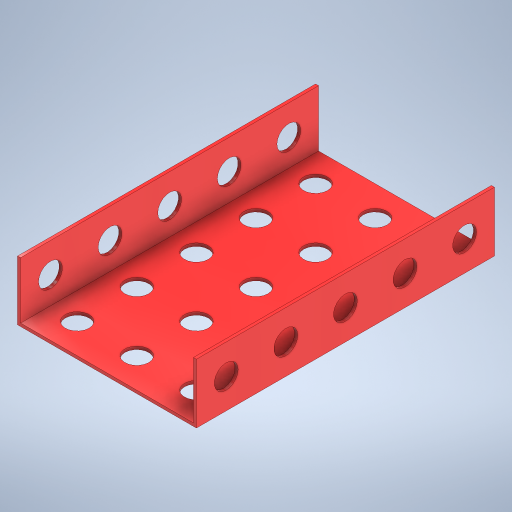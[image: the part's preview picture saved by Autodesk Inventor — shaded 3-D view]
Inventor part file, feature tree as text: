
AUTODESK INVENTOR PART (.ipt)
format: ipt  version: 2024 (Build 280153000, 153)  size: 333,312 bytes
history: native  units: mm
features: extrude x3, sketch x3, pattern_linear x2, other x1
ambient origin geometry x8: Origin, YZ Plane, XZ Plane, XY Plane, X Axis, Y Axis, Z Axis, Center Point
bodies: Body1 (feature_tree)
feature tree (9):
  other  "Těleso1"
  extrude  "Vysunutí1"  Depth=15.0mm
  extrude  "Vysunutí2"  Depth=15.0mm
  pattern_linear  "Obdélníkové pole1"  Spacing1=0.5mm  [1 undecoded]
  extrude  "Vysunutí3"  Depth=0.5mm
  pattern_linear  "Obdélníkové pole2"  Spacing1=0.5mm  [1 undecoded]
  sketch  "Náčrt1"
  sketch  "Náčrt2"
  sketch  "Náčrt3"
note: 2 required parameter values undecoded (feature->parameter linkage not recoverable at this tier; creation-order binding heuristic only, values carry confidence <= 0.55)
